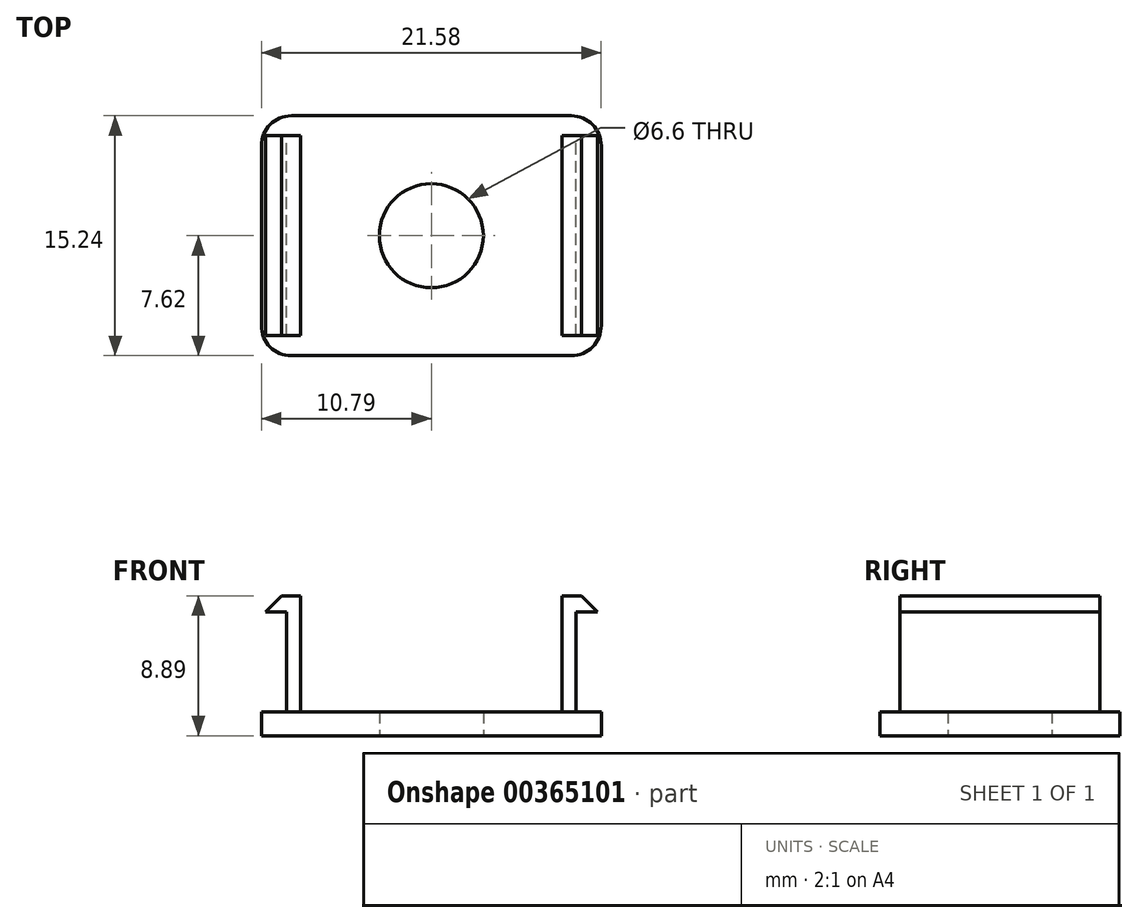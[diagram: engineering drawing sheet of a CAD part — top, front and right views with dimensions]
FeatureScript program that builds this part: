
annotation { "Feature Type Name" : "Feature", "Feature Type Description" : "" }
export const myFeature = defineFeature(function(context is Context, id is Id, definition is map)
    precondition{}
    {
        {
            var Q0;
            Q0=qCreatedBy(makeId("Top.planeOp"),FACE);
            var sketch = newSketch(context, id + "F0", { "sketchPlane" : qUnion([Q0])});
            skLineSegment(sketch, "E0.bottom", {"start": v(10.8, -7.62) * mm, "end": v(-10.8, -7.62) * mm});
            skLineSegment(sketch, "E0.top", {"start": v(10.8, 7.62) * mm, "end": v(-10.8, 7.62) * mm});
            skLineSegment(sketch, "E0.left", {"start": v(10.8, -7.62) * mm, "end": v(10.8, 7.62) * mm});
            skLineSegment(sketch, "E0.right", {"start": v(-10.8, -7.62) * mm, "end": v(-10.8, 7.62) * mm});
            skPoint(sketch, "E0.middle", {"position": v(0, 0) * mm});
            skCircle(sketch, "E1", {"center": v(0, 0) * mm, "radius": 3.3 * mm});
            skLineSegment(sketch, "E2.bottom", {"start": v(-8.3, -6.35) * mm, "end": v(-9.2, -6.35) * mm});
            skLineSegment(sketch, "E2.top", {"start": v(-8.3, 6.35) * mm, "end": v(-9.2, 6.35) * mm});
            skLineSegment(sketch, "E2.left", {"start": v(-8.3, -6.35) * mm, "end": v(-8.3, 6.35) * mm});
            skLineSegment(sketch, "E2.right", {"start": v(-9.2, -6.35) * mm, "end": v(-9.2, 6.35) * mm});
            skPoint(sketch, "E2.middle", {"position": v(-8.75, 0) * mm});
            skLineSegment(sketch, "E3.MirrorCS", {"start": v(8.3, -6.35) * mm, "end": v(8.3, 6.35) * mm});
            skLineSegment(sketch, "E4.MirrorCS", {"start": v(8.3, 6.35) * mm, "end": v(9.2, 6.35) * mm});
            skLineSegment(sketch, "E5.MirrorCS", {"start": v(8.3, -6.35) * mm, "end": v(9.2, -6.35) * mm});
            skPoint(sketch, "E6.MirrorP", {"position": v(8.75, 0) * mm});
            skLineSegment(sketch, "E7.MirrorCS", {"start": v(9.2, -6.35) * mm, "end": v(9.2, 6.35) * mm});
            skSolve(sketch);
        }
        {
            var Q0;
            Q0=makeQuery(id+"F0.imprint","IMPRINT",FACE,{"disambiguationData":[TD([[makeQuery(id+"F0.imprint","IMPRINT",EDGE,{"derivedFrom":sQuery(id+"F0.wireOp",EDGE,"E0.bottom")}),-1.0]])]});
            extrude(context, id + "F1", {"entities" : qUnion([Q0]), "depth" : 1.52 * mm});
        }
        {
            var Q0;
            Q0=makeQuery(id+"F0.imprint","IMPRINT",FACE,{"disambiguationData":[TD([[makeQuery(id+"F0.imprint","IMPRINT",EDGE,{"derivedFrom":sQuery(id+"F0.wireOp",EDGE,"E2.bottom")}),-1.0]])]});
            var Q1;
            Q1=makeQuery(id+"F0.imprint","IMPRINT",FACE,{"disambiguationData":[TD([[makeQuery(id+"F0.imprint","IMPRINT",EDGE,{"derivedFrom":sQuery(id+"F0.wireOp",EDGE,"E3.MirrorCS")}),-1.0]])]});
            extrude(context, id + "F2", {"entities" : qUnion([Q0, Q1]), "operationType" : NewBodyOperationType.ADD, "depth" : 8.9 * mm});
        }
        {
            var Q0;
            Q0=makeQuery(id+"F2.opExtrude","SWEPT_FACE",FACE,{"disambiguationData":[OSD([sQuery(id+"F0.wireOp",EDGE,"E2.right")])]});
            var sketch = newSketch(context, id + "F3", { "sketchPlane" : qUnion([Q0])});
            skLineSegment(sketch, "E8.bottom", {"start": v(-6.35, 8.9) * mm, "end": v(6.35, 8.9) * mm});
            skLineSegment(sketch, "E8.top", {"start": v(-6.35, 7.87) * mm, "end": v(6.35, 7.87) * mm});
            skLineSegment(sketch, "E8.left", {"start": v(-6.35, 8.9) * mm, "end": v(-6.35, 7.87) * mm});
            skLineSegment(sketch, "E8.right", {"start": v(6.35, 8.9) * mm, "end": v(6.35, 7.87) * mm});
            skSolve(sketch);
        }
        {
            var Q0;
            Q0=makeQuery(id+"F2.opExtrude","SWEPT_FACE",FACE,{"disambiguationData":[OSD([sQuery(id+"F0.wireOp",EDGE,"E7.MirrorCS")])]});
            var sketch = newSketch(context, id + "F4", { "sketchPlane" : qUnion([Q0])});
            skLineSegment(sketch, "E9.0", {"start": v(6.35, 7.87) * mm, "end": v(-6.35, 7.87) * mm});
            skLineSegment(sketch, "E10.0", {"start": v(6.35, 8.9) * mm, "end": v(6.35, 7.87) * mm});
            skLineSegment(sketch, "E11.0", {"start": v(6.35, 8.9) * mm, "end": v(-6.35, 8.9) * mm});
            skLineSegment(sketch, "E12.0", {"start": v(-6.35, 8.9) * mm, "end": v(-6.35, 7.87) * mm});
            skSolve(sketch);
        }
        {
            var Q0;
            Q0=makeQuery(id+"F3.imprint","IMPRINT",FACE,{"disambiguationData":[TD([[makeQuery(id+"F3.imprint","IMPRINT",EDGE,{"derivedFrom":sQuery(id+"F3.wireOp",EDGE,"E8.bottom")}),1.0]])]});
            extrude(context, id + "F5", {"entities" : qUnion([Q0]), "operationType" : NewBodyOperationType.ADD, "depth" : 1.6 * mm});
        }
        {
            var Q0;
            Q0=makeQuery(id+"F4.imprint","IMPRINT",FACE,{"disambiguationData":[TD([[makeQuery(id+"F4.imprint","IMPRINT",EDGE,{"derivedFrom":sQuery(id+"F4.wireOp",EDGE,"E9.0")}),-1.0]])]});
            extrude(context, id + "F6", {"entities" : qUnion([Q0]), "operationType" : NewBodyOperationType.ADD, "depth" : 1.6 * mm});
        }
        {
            var Q0;
            Q0=makeQuery(id+"F5.opExtrude","CAP_EDGE",EDGE,{"disambiguationData":[OSD([sQuery(id+"F3.wireOp",EDGE,"E8.bottom")])],"isStart":false});
            var Q1;
            Q1=makeQuery(id+"F6.opExtrude","CAP_EDGE",EDGE,{"disambiguationData":[OSD([sQuery(id+"F4.wireOp",EDGE,"E11.0")])],"isStart":false});
            chamfer(context, id + "F7", {"entities" : qUnion([Q0, Q1]), "width" : 1.27 * mm, "tangentPropagation" : true});
        }
        {
            var Q0;
            Q0=makeQuery(id+"F1.opExtrude","SWEPT_EDGE",EDGE,{"disambiguationData":[OSD([sQuery(id+"F0.wireOp",EDGE,"E0.bottom"),sQuery(id+"F0.wireOp",EDGE,"E0.left")])]});
            var Q1;
            Q1=makeQuery(id+"F1.opExtrude","SWEPT_EDGE",EDGE,{"disambiguationData":[OSD([sQuery(id+"F0.wireOp",EDGE,"E0.top"),sQuery(id+"F0.wireOp",EDGE,"E0.left")])]});
            var Q2;
            Q2=makeQuery(id+"F1.opExtrude","SWEPT_EDGE",EDGE,{"disambiguationData":[OSD([sQuery(id+"F0.wireOp",EDGE,"E0.top"),sQuery(id+"F0.wireOp",EDGE,"E0.right")])]});
            var Q3;
            Q3=makeQuery(id+"F1.opExtrude","SWEPT_EDGE",EDGE,{"disambiguationData":[OSD([sQuery(id+"F0.wireOp",EDGE,"E0.bottom"),sQuery(id+"F0.wireOp",EDGE,"E0.right")])]});
            fillet(context, id + "F8", {"entities" : qUnion([Q0, Q1, Q2, Q3]), "radius" : 1.9 * mm, "tangentPropagation" : true, "allowEdgeOverflow" : false});
        }
    });
